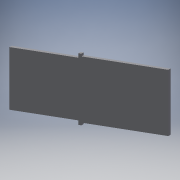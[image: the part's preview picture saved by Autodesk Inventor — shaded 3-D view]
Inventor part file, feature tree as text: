
AUTODESK INVENTOR PART (.ipt)
format: ipt  version: 2018.3 (Build 223284000, 284)  size: 1,153,024 bytes
history: native  units: mm
features: extrude x5, sketch x5
ambient origin geometry x8: Origin, YZ Plane, XZ Plane, XY Plane, X Axis, Y Axis, Z Axis, Center Point
bodies: Body1 (feature_tree)
feature tree (10):
  extrude  "Extrusion6"  Depth=150.0mm
  extrude  "Extrusion8"  Depth=3.0mm
  extrude  "Extrusion9"  Depth=3.0mm
  extrude  "Extrusion10"  Depth=2.0mm TaperAngle=0.0deg
  extrude  "Extrusion11"  Depth=3.0mm
  sketch  "Sketch6"  dims[d18=3.0mm d19=150.0mm]
  sketch  "Sketch8"  dims[d20=120.0deg d21=3.0mm]
  sketch  "Sketch9"  dims[d22=70.0mm d23=0.0mm d27=3.0mm]
  sketch  "Sketch10"  dims[d28=5.0mm d29=0.0mm d30=2.0mm d31=0.0mm]
  sketch  "Sketch11"  dims[d32=65.0mm d33=3.0mm d34=5.0mm d35=0.0mm d36=2.0mm d37=0.0mm]
